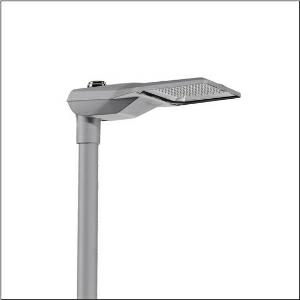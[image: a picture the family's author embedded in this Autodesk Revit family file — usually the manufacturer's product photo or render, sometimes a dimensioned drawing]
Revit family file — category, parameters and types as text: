
# Revit family: streetlight_sl_21_midi___st1_0a_5xe7d47n08mb_32fc
name_source: partatom
category: Lighting Fixtures
units: mm (PartAtom-declared; Revit-internal decimal feet)

## family parameters
Cut with Voids When Loaded = No
Host = Face
Light Source = No
Part Type = Normal
Room Calculation Point = No
Round Connector Dimension = Use Diameter
Shared = No

## types (1)
- --- (1 x LED, 20180 lm, 147 W, 4000K)
    Apparent Load = 147 VA
    CIE Flux Codes = 37 72 97 100 100
    Color Rendering = 70
    Color Temperature = 4000K
    Default Elevation = 1800 mm
    Description = Streetlight SL 21 midi, mast luminaire, primary light control with lens, of PMMA, primary optical cover: cover, of toughened safety glass, transparent, light distribution: ST1.0a, light emission: direct distribution, primary light characteristic: asymmetric, installation type: side-entry, LED, 3G 2.5mm², High Power LED, rated luminous flux: 20.180lm, luminous efficacy: 137lm/W, light colour: 740, colour temperature: 4000K, control gear: NEMA (7pin), control: overheat protection, pre-setting: linear dimming characteristic, constant luminous flux control, time-dependent luminous flux control, flexible luminous flux parameterisation, mains connection: 220..240V, AC, 50/60Hz, connection cable pre-assembled, cable length: 12,5m, wiring characteristics: H05VV-F, start of lifetime: 147W, end of service life: 155W, reduction: 65W, luminaire housing, of diecast aluminium (EN AC-44300), powder-coated, Siteco® metallic grey (DB 702S), corrosivity category C5 mid according to DIN EN ISO 12944, multi-level sealing system, sealing non-destructively replaceable, inclination adjustable: 0°, 5°, 10°, 15°, length: 644mm, width: 335mm, height: 110mm, spigot size: 42mm (side-entry), mounting height: 4..8m, protection rating (complete): IP66, insulation class (complete): insulation class I (protective earthing), certification: CE, ENEC, ENEC+, VDE, impact resistance: IK10, permissible operating ambient temperature for outdoor applications: -40..+50°C, standard-compliant lighting for roads and squares, packaging unit: 1 piece

Light Distribution: ST1.0a
    Height = 111 mm
    Lamp = 1 x LED
    Lamp Light Flux = 20180 lm
    Lamp Power = 147 W
    Lamp count = 1
    Length = 644 mm
    Luminous efficacy = 137 lm/W
    Manufacturer = Siteco
    ModVariant = No
    Model = 5XE7D47N08MB
    Number of Poles = 1
    OnlyDefault = Yes
    Power Factor = 1
    Product Name = Streetlight SL 21 midi | ST1.0a
    Product group = mast luminaire | pylon top
    ProductGroupID = 6100
    Protection Class = Protection class I
    Protection Degree = IP 66
    RLX_Detail_Level = 1
    RLX_Emergency_Light_Flux = 0 lm
    RLX_Emergency_Type = 0
    RLX_Emergency_Type_DB = No
    RlxData = <blob elided: 26545 chars, md5=125cfa74>
    Socket = socket
    Standby Power = 0 W
    System Light Flux = 20180 lm
    System Power = 147 W
    Type Comments = factory setting: luminous flux: 100 % | dim-lin: 254 | 750 mA
    Type Image = l_1294377.jpg
    URL = http://relux.com
    VarID = @adj_135970
    Voltage = 0 V
    Weight = 0.00 kg
    Width = 336 mm

## geometry (parser evidence)
native form markers: Blend x4, Sweep x10
no freeform markers — native parametric forms only
